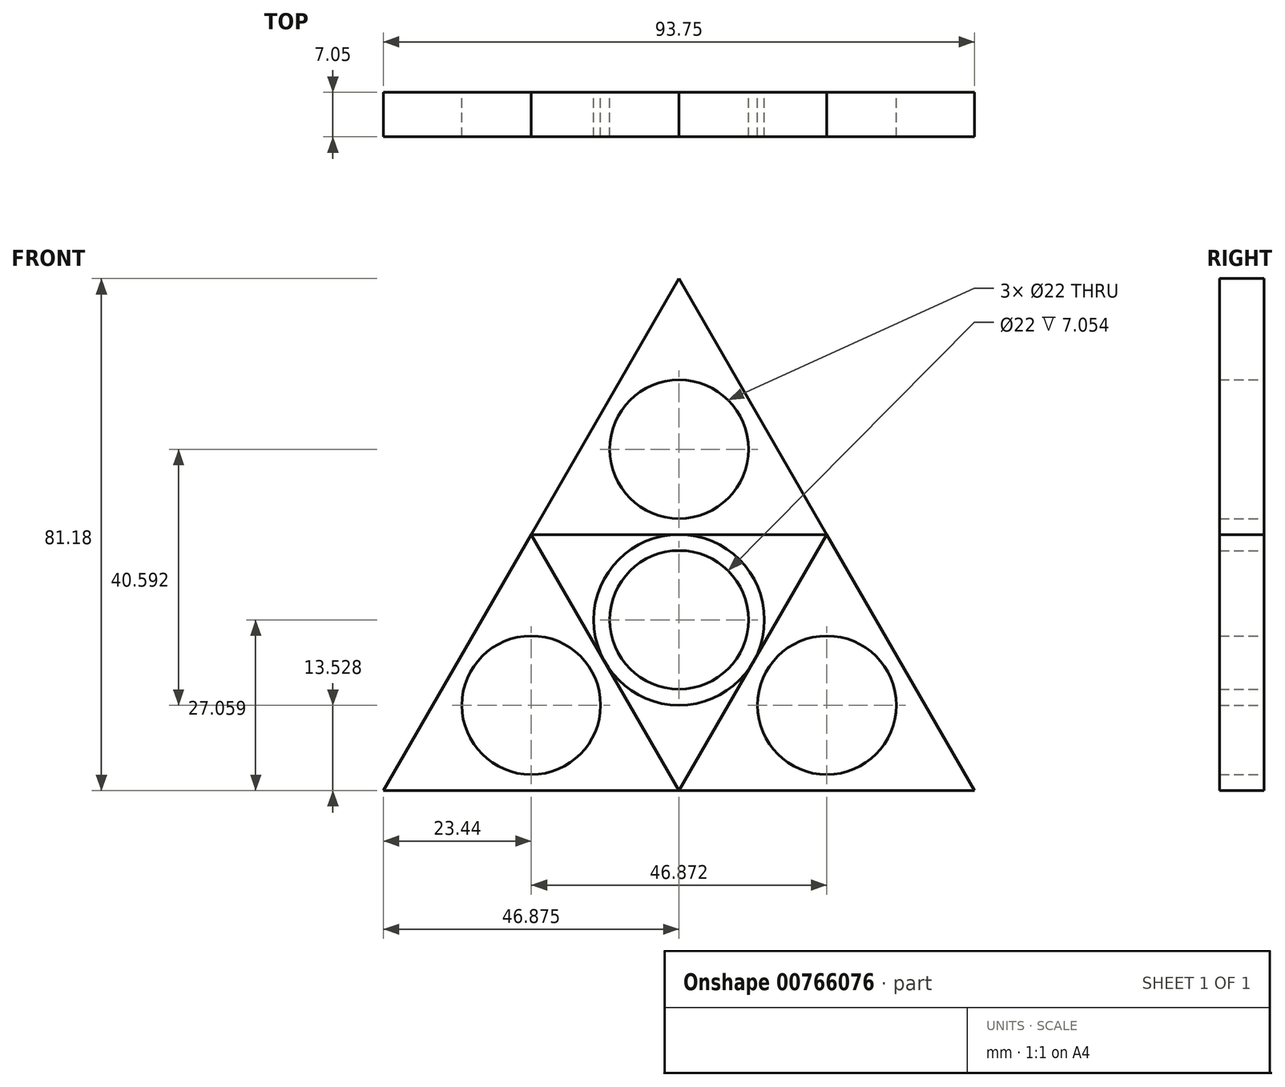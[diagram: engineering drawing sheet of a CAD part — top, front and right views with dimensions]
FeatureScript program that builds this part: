
annotation { "Feature Type Name" : "Feature", "Feature Type Description" : "" }
export const myFeature = defineFeature(function(context is Context, id is Id, definition is map)
    precondition{}
    {
        {
            var Q0;
            Q0=qCreatedBy(makeId("Front.planeOp"),FACE);
            var sketch = newSketch(context, id + "F0", { "sketchPlane" : qUnion([Q0])});
            skLineSegment(sketch, "E0", {"start": v(-23.16, 22.72) * mm, "end": v(-46.6, -17.87) * mm});
            skLineSegment(sketch, "E1", {"start": v(-46.6, -17.87) * mm, "end": v(0.28, -17.87) * mm});
            skLineSegment(sketch, "E2", {"start": v(0.28, -17.87) * mm, "end": v(-23.16, 22.72) * mm});
            skLineSegment(sketch, "E3", {"start": v(-23.16, 22.72) * mm, "end": v(23.71, 22.72) * mm});
            skLineSegment(sketch, "E4", {"start": v(23.71, 22.72) * mm, "end": v(0.28, 63.31) * mm});
            skLineSegment(sketch, "E5", {"start": v(0.28, 63.31) * mm, "end": v(-23.16, 22.72) * mm});
            skLineSegment(sketch, "E6", {"start": v(23.71, 22.72) * mm, "end": v(0.28, -17.87) * mm});
            skLineSegment(sketch, "E7", {"start": v(47.15, -17.87) * mm, "end": v(23.71, 22.72) * mm});
            skLineSegment(sketch, "E8", {"start": v(0.28, -17.87) * mm, "end": v(47.15, -17.87) * mm});
            skLineSegment(sketch, "E9", {"start": v(0.28, 22.72) * mm, "end": v(-23.16, 22.72) * mm});
            skCircle(sketch, "E10", {"center": v(0.28, 9.19) * mm, "radius": 13.53 * mm});
            skCircle(sketch, "E11", {"center": v(0.28, 9.19) * mm, "radius": 11 * mm});
            skLineSegment(sketch, "E12", {"start": v(-23.16, -17.87) * mm, "end": v(-46.6, -17.87) * mm});
            skCircle(sketch, "E13", {"center": v(-23.16, -4.34) * mm, "radius": 11 * mm});
            skCircle(sketch, "E14", {"center": v(23.71, -4.34) * mm, "radius": 11 * mm});
            skCircle(sketch, "E15", {"center": v(0.28, 36.25) * mm, "radius": 11 * mm});
            skSolve(sketch);
        }
        {
            var Q0;
            Q0=makeQuery(id+"F0.imprint","IMPRINT",FACE,{"disambiguationData":[TD([[makeQuery(id+"F0.imprint","IMPRINT",EDGE,{"derivedFrom":sQuery(id+"F0.wireOp",EDGE,"E3")}),1.0]])]});
            var Q1;
            {var subQ0=sQuery(id+"F0.wireOp",EDGE,"E0");Q1=makeQuery(id+"F0.imprint","IMPRINT",FACE,{"disambiguationData":[TD([[makeQuery(id+"F0.imprint","IMPRINT",EDGE,{"derivedFrom":subQ0}),1.0]])]});}
            var Q2;
            {var subQ0=sQuery(id+"F0.wireOp",EDGE,"E10");var subQ2=makeQuery(id+"F0.imprint","INTERSECT",VERTEX,{"derivedFrom":[sQuery(id+"F0.wireOp",EDGE,"E2"),subQ0]});Q2=makeQuery(id+"F0.imprint","IMPRINT",FACE,{"disambiguationData":[TD([[makeQuery(id+"F0.imprint","IMPRINT",EDGE,{"disambiguationData":[TD([[subQ2,-1.0]])],"derivedFrom":subQ0}),1.0]])]});}
            var Q3;
            {var subQ0=sQuery(id+"F0.wireOp",EDGE,"E7");Q3=makeQuery(id+"F0.imprint","IMPRINT",FACE,{"disambiguationData":[TD([[makeQuery(id+"F0.imprint","IMPRINT",EDGE,{"derivedFrom":subQ0}),1.0]])]});}
            extrude(context, id + "F1", {"entities" : qUnion([Q0, Q1, Q2, Q3]), "depth" : 7.05 * mm, "offsetDistance" : 25.4 * mm});
        }
    });
